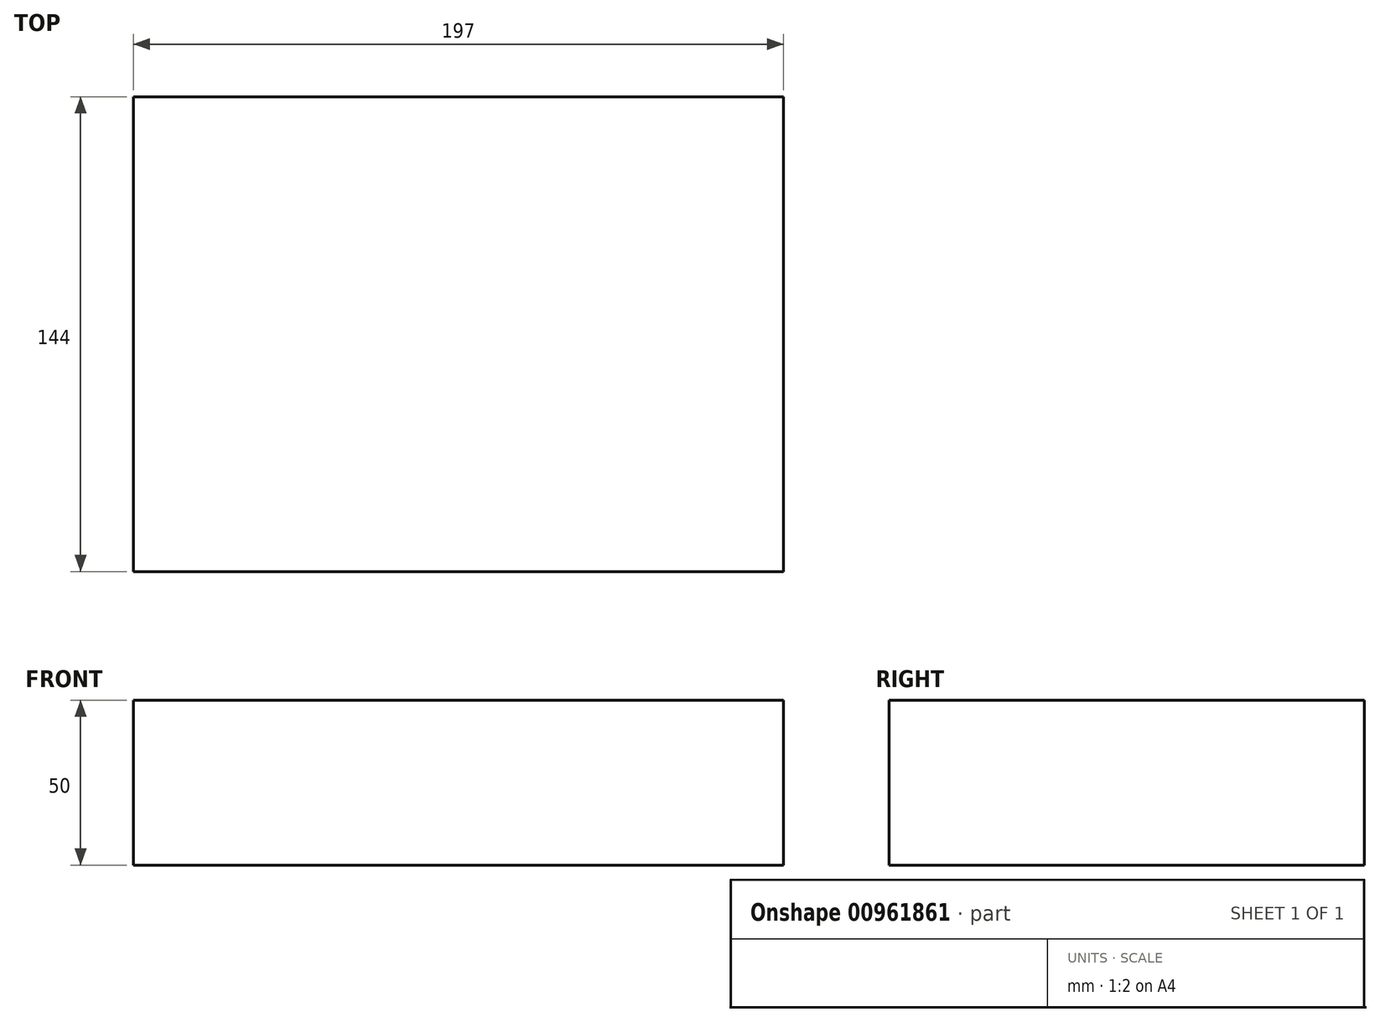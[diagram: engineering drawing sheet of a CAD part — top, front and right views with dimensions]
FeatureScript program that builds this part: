
annotation { "Feature Type Name" : "Feature", "Feature Type Description" : "" }
export const myFeature = defineFeature(function(context is Context, id is Id, definition is map)
    precondition{}
    {
        {
            var Q0;
            Q0=qCreatedBy(makeId("Top.planeOp"),FACE);
            var sketch = newSketch(context, id + "F0", { "sketchPlane" : qUnion([Q0])});
            skLineSegment(sketch, "E0.bottom", {"start": v(-197, 124.62) * mm, "end": v(0, 124.62) * mm});
            skLineSegment(sketch, "E0.top", {"start": v(-197, -19.38) * mm, "end": v(0, -19.38) * mm});
            skLineSegment(sketch, "E0.left", {"start": v(-197, 124.62) * mm, "end": v(-197, -19.38) * mm});
            skLineSegment(sketch, "E0.right", {"start": v(0, 124.62) * mm, "end": v(0, -19.38) * mm});
            skSolve(sketch);
        }
        {
            var Q0;
            Q0 = qSketchRegion(id + "F0", true);
            extrude(context, id + "F1", {"entities" : qUnion([Q0]), "depth" : 50 * mm, "offsetDistance" : 25 * mm});
        }
    });
